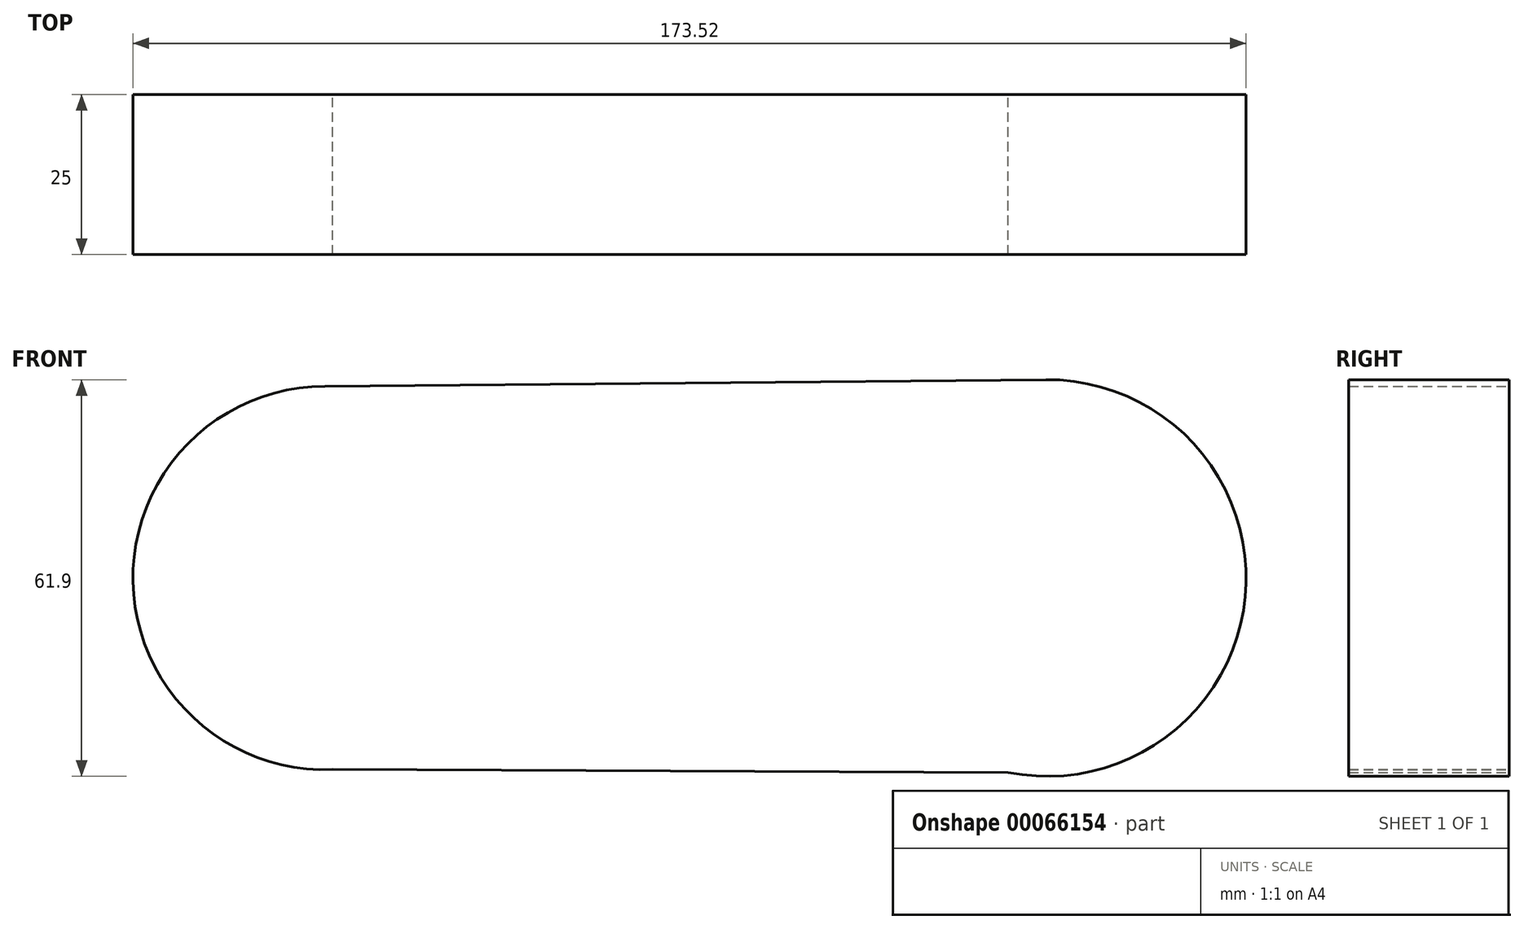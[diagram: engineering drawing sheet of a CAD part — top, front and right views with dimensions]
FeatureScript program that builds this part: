
annotation { "Feature Type Name" : "Feature", "Feature Type Description" : "" }
export const myFeature = defineFeature(function(context is Context, id is Id, definition is map)
    precondition{}
    {
        {
            var Q0;
            Q0=qCreatedBy(makeId("Front.planeOp"),FACE);
            var sketch = newSketch(context, id + "F0", { "sketchPlane" : qUnion([Q0])});
            skCircle(sketch, "E0", {"center": v(-64.33, 0) * mm, "radius": 29.9 * mm});
            skCircle(sketch, "E1", {"center": v(48.34, 0) * mm, "radius": 30.95 * mm});
            skLineSegment(sketch, "E2", {"start": v(-64.33, 29.9) * mm, "end": v(55.66, 31.02) * mm});
            skLineSegment(sketch, "E3", {"start": v(-65.79, -29.86) * mm, "end": v(54.21, -30.39) * mm});
            skSolve(sketch);
        }
        {
            var Q0;
            Q0 = qSketchRegion(id + "F0", true);
            extrude(context, id + "F1", {"entities" : qUnion([Q0]), "depth" : 25 * mm});
        }
    });
